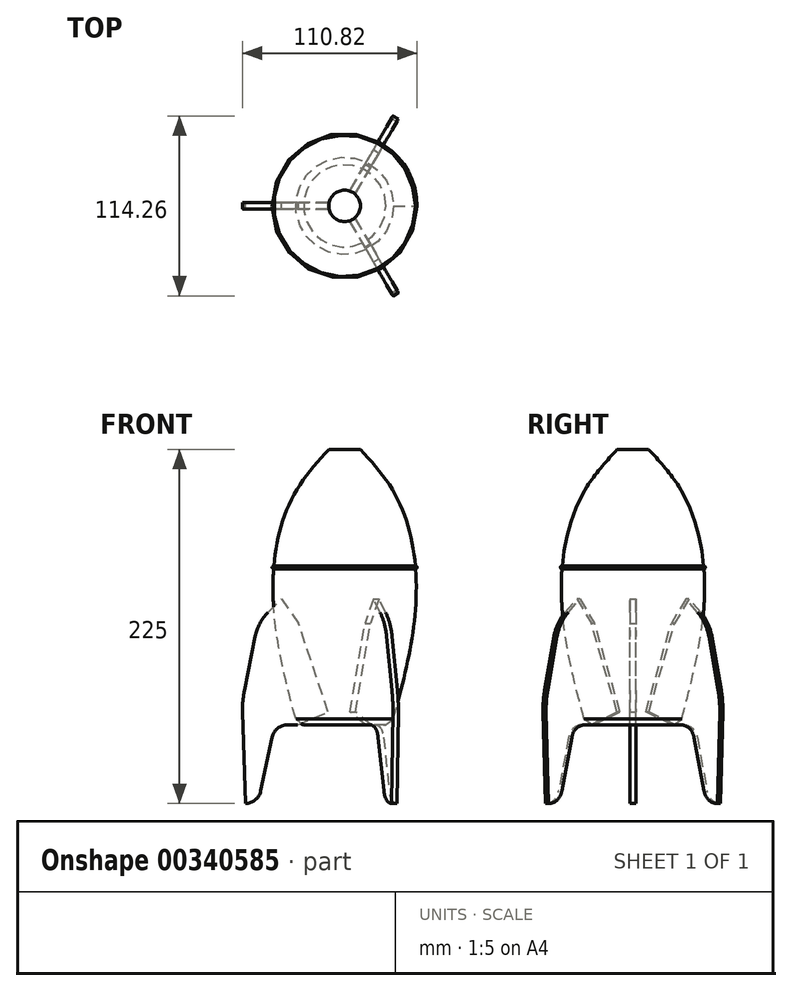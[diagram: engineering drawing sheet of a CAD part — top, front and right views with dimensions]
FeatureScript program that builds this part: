
annotation { "Feature Type Name" : "Feature", "Feature Type Description" : "" }
export const myFeature = defineFeature(function(context is Context, id is Id, definition is map)
    precondition{}
    {
        {
            var Q0;
            Q0=qCreatedBy(makeId("Top.planeOp"),FACE);
            var sketch = newSketch(context, id + "F0", { "sketchPlane" : qUnion([Q0])});
            skCircle(sketch, "E0", {"center": v(0, 0) * mm, "radius": 30 * mm});
            skSolve(sketch);
        }
        {
            var Q0;
            Q0=qCreatedBy(makeId("Top.planeOp"),FACE);
            cPlane(context, id + "F1", {"entities" : qUnion([Q0]), "cplaneType" : CPlaneType.OFFSET, "offset" : 100 * mm, "width" : 150 * mm, "height" : 150 * mm});
        }
        {
            var Q0;
            Q0=qCreatedBy(id+"F1.planeOp",FACE);
            var sketch = newSketch(context, id + "F2", { "sketchPlane" : qUnion([Q0])});
            skPoint(sketch, "E1.0", {"position": v(0, 0) * mm});
            skCircle(sketch, "E2", {"center": v(0, 0) * mm, "radius": 45 * mm});
            skSolve(sketch);
        }
        {
            var Q0;
            Q0=qCreatedBy(id+"F1.planeOp",FACE);
            cPlane(context, id + "F3", {"entities" : qUnion([Q0]), "cplaneType" : CPlaneType.OFFSET, "offset" : 50 * mm, "width" : 150 * mm, "height" : 150 * mm});
        }
        {
            var Q0;
            Q0=qCreatedBy(id+"F3.planeOp",FACE);
            cPlane(context, id + "F4", {"entities" : qUnion([Q0]), "cplaneType" : CPlaneType.OFFSET, "offset" : 25 * mm, "width" : 150 * mm, "height" : 150 * mm});
        }
        {
            var Q0;
            Q0=qCreatedBy(id+"F3.planeOp",FACE);
            var sketch = newSketch(context, id + "F5", { "sketchPlane" : qUnion([Q0])});
            skPoint(sketch, "E3.0", {"position": v(0, 0) * mm});
            skCircle(sketch, "E4", {"center": v(0, 0) * mm, "radius": 30 * mm});
            skSolve(sketch);
        }
        {
            var Q0;
            Q0=qCreatedBy(id+"F4.planeOp",FACE);
            var sketch = newSketch(context, id + "F6", { "sketchPlane" : qUnion([Q0])});
            skPoint(sketch, "E5.0", {"position": v(0, 0) * mm});
            skCircle(sketch, "E6", {"center": v(0, 0) * mm, "radius": 10 * mm});
            skSolve(sketch);
        }
        {
            var Q0;
            Q0=makeQuery(id+"F0.imprint","IMPRINT",FACE,{"disambiguationData":[TD([[makeQuery(id+"F0.imprint","IMPRINT",EDGE,{"derivedFrom":sQuery(id+"F0.wireOp",EDGE,"E0")}),1.0]])]});
            var Q1;
            Q1=makeQuery(id+"F2.imprint","IMPRINT",FACE,{"disambiguationData":[TD([[makeQuery(id+"F2.imprint","IMPRINT",EDGE,{"derivedFrom":sQuery(id+"F2.wireOp",EDGE,"E2")}),1.0]])]});
            var Q2;
            Q2=makeQuery(id+"F5.imprint","IMPRINT",FACE,{"disambiguationData":[TD([[makeQuery(id+"F5.imprint","IMPRINT",EDGE,{"derivedFrom":sQuery(id+"F5.wireOp",EDGE,"E4")}),1.0]])]});
            var Q3;
            Q3=makeQuery(id+"F6.imprint","IMPRINT",FACE,{"disambiguationData":[TD([[makeQuery(id+"F6.imprint","IMPRINT",EDGE,{"derivedFrom":sQuery(id+"F6.wireOp",EDGE,"E6")}),1.0]])]});
            loft(context, id + "F7", {"sheetProfilesArray" : [{ "sheetProfileEntities" : qUnion([Q0]) }, { "sheetProfileEntities" : qUnion([Q1]) }, { "sheetProfileEntities" : qUnion([Q2]) }, { "sheetProfileEntities" : qUnion([Q3]) }]});
        }
        {
            var Q0;
            Q0=qCreatedBy(makeId("Right.planeOp"),FACE);
            var sketch = newSketch(context, id + "F8", { "sketchPlane" : qUnion([Q0])});
            skLineSegment(sketch, "E7.0", {"start": v(-45, 100) * mm, "end": v(45, 100) * mm});
            skCircle(sketch, "E8", {"center": v(45, 100) * mm, "radius": 1 * mm});
            skSolve(sketch);
        }
        {
            var Q0;
            Q0=makeQuery(id+"F8.imprint","IMPRINT",FACE,{"disambiguationData":[TD([[makeQuery(id+"F8.imprint","IMPRINT",EDGE,{"derivedFrom":sQuery(id+"F8.wireOp",EDGE,"E8")}),1.0]])]});
            var Q1;
            Q1=sQuery(id+"F2.wireOp",EDGE,"E2");
            sweep(context, id + "F9", {"operationType" : NewBodyOperationType.ADD, "profiles" : qUnion([Q0]), "path" : qUnion([Q1])});
        }
        {
            var Q0;
            Q0=qCreatedBy(makeId("Front.planeOp"),FACE);
            var sketch = newSketch(context, id + "F10", { "sketchPlane" : qUnion([Q0])});
            skLineSegment(sketch, "E9.0", {"start": v(-30, 0) * mm, "end": v(30, 0) * mm});
            skLineSegment(sketch, "E10", {"start": v(-30, 0) * mm, "end": v(-10.54, 8.21) * mm});
            skLineSegment(sketch, "E11", {"start": v(-10.54, 8.21) * mm, "end": v(-29.25, 64.25) * mm});
            skLineSegment(sketch, "E12", {"start": v(-30, 0) * mm, "end": v(-36.22, 0) * mm});
            skLineSegment(sketch, "E13", {"start": v(-46, -7.9) * mm, "end": v(-55, -50) * mm});
            skLineSegment(sketch, "E14", {"start": v(-55, -50) * mm, "end": v(-63, -50) * mm});
            skLineSegment(sketch, "E15", {"start": v(-63, -50) * mm, "end": v(-65, 15) * mm});
            skLineSegment(sketch, "E16", {"start": v(-65, 15) * mm, "end": v(-55, 65) * mm});
            skLineSegment(sketch, "E17", {"start": v(-55, 65) * mm, "end": v(-40, 80) * mm});
            skLineSegment(sketch, "E18", {"start": v(-40, 80) * mm, "end": v(-29.25, 64.25) * mm});
            skPoint(sketch, "E19.visualSharp", {"position": v(-44.3, 0) * mm});
            skArc(sketch, "E19.filletArc", {"start": v(-36.22, 0) * mm, "mid": v(-42.5, -2.22) * mm, "end": v(-46, -7.9) * mm});
            skSolve(sketch);
        }
        {
            var Q0;
            Q0 = qSketchRegion(id + "F10", true);
            extrude(context, id + "F11", {"entities" : qUnion([Q0]), "endBound" : BoundingType.SYMMETRIC, "depth" : 4 * mm});
        }
        {
            var Q0;
            Q0=makeQuery(id+"F11.opExtrude","SWEPT_EDGE",EDGE,{"disambiguationData":[OSD([sQuery(id+"F10.wireOp",EDGE,"E16"),sQuery(id+"F10.wireOp",EDGE,"E17")])]});
            fillet(context, id + "F12", {"entities" : qUnion([Q0]), "radius" : 30 * mm, "tangentPropagation" : true, "allowEdgeOverflow" : false});
        }
        {
            var Q0;
            Q0=makeQuery(id+"F11.opExtrude","SWEPT_EDGE",EDGE,{"disambiguationData":[OSD([sQuery(id+"F10.wireOp",EDGE,"E15"),sQuery(id+"F10.wireOp",EDGE,"E16")])]});
            fillet(context, id + "F13", {"entities" : qUnion([Q0]), "radius" : 60 * mm, "tangentPropagation" : true, "allowEdgeOverflow" : false});
        }
        {
            var Q0;
            Q0=makeQuery(id+"F11.opExtrude","SWEPT_EDGE",EDGE,{"disambiguationData":[OSD([sQuery(id+"F10.wireOp",EDGE,"E13"),sQuery(id+"F10.wireOp",EDGE,"E14")])]});
            fillet(context, id + "F14", {"entities" : qUnion([Q0]), "radius" : 10 * mm, "tangentPropagation" : true, "allowEdgeOverflow" : false});
        }
        {
            var Q0;
            Q0=makeQuery(id+"F11.opExtrude","SWEPT_BODY",BODY,{"disambiguationData":[OSD([sQuery(id+"F10.wireOp",EDGE,"E10"),sQuery(id+"F10.wireOp",EDGE,"E11"),sQuery(id+"F10.wireOp",EDGE,"E12"),sQuery(id+"F10.wireOp",EDGE,"E13"),sQuery(id+"F10.wireOp",EDGE,"E14"),sQuery(id+"F10.wireOp",EDGE,"E15"),sQuery(id+"F10.wireOp",EDGE,"E16"),sQuery(id+"F10.wireOp",EDGE,"E17"),sQuery(id+"F10.wireOp",EDGE,"E18"),sQuery(id+"F10.wireOp",EDGE,"E19.filletArc")])]});
            var Q1;
            Q1=sQuery(id+"F2.wireOp",EDGE,"E2");
            circularPattern(context, id + "F15", {"entities" : qUnion([Q0]), "axis" : qUnion([Q1]), "angle" : 360 * degree, "instanceCount" : 3, "equalSpace" : true});
        }
        {
            var Q0;
            Q0=makeQuery(id+"F7.opLoft","MID_CAP_EDGE",EDGE,{"disambiguationData":[OSD([sQuery(id+"F0.wireOp",EDGE,"E0")])],"capPos":0.0});
            chamfer(context, id + "F16", {"entities" : qUnion([Q0]), "width" : 5 * mm, "tangentPropagation" : true});
        }
    });
